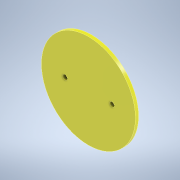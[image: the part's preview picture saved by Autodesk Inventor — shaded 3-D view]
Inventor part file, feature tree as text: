
AUTODESK INVENTOR PART (.ipt)
format: ipt  version: 2021 (Build 250183000, 183)  size: 101,888 bytes
history: native  units: mm
features: sketch x2, other x1, extrude x1, hole x1
ambient origin geometry x8: Origin, YZ Plane, XZ Plane, XY Plane, X Axis, Y Axis, Z Axis, Center Point
bodies: Body1 (feature_tree)
feature tree (5):
  other  "Sólido1"
  extrude  "Extrusão1"  Depth=2.0mm TaperAngle=0.0deg
  hole  "Furo1"  [1 undecoded]
  sketch  "Esboço1"  dims[d0=60.0mm d1=2.0mm d2=0.0mm]
  sketch  "Esboço2"  dims[d3=15.0mm d4=15.0mm d5=3.0mm d6=6.0mm d7=4.0mm d8=2.0mm d9=90.0deg d10=8.0mm d11=20.594885mm]
note: 1 required parameter value undecoded (feature->parameter linkage not recoverable at this tier; creation-order binding heuristic only, values carry confidence <= 0.55)
